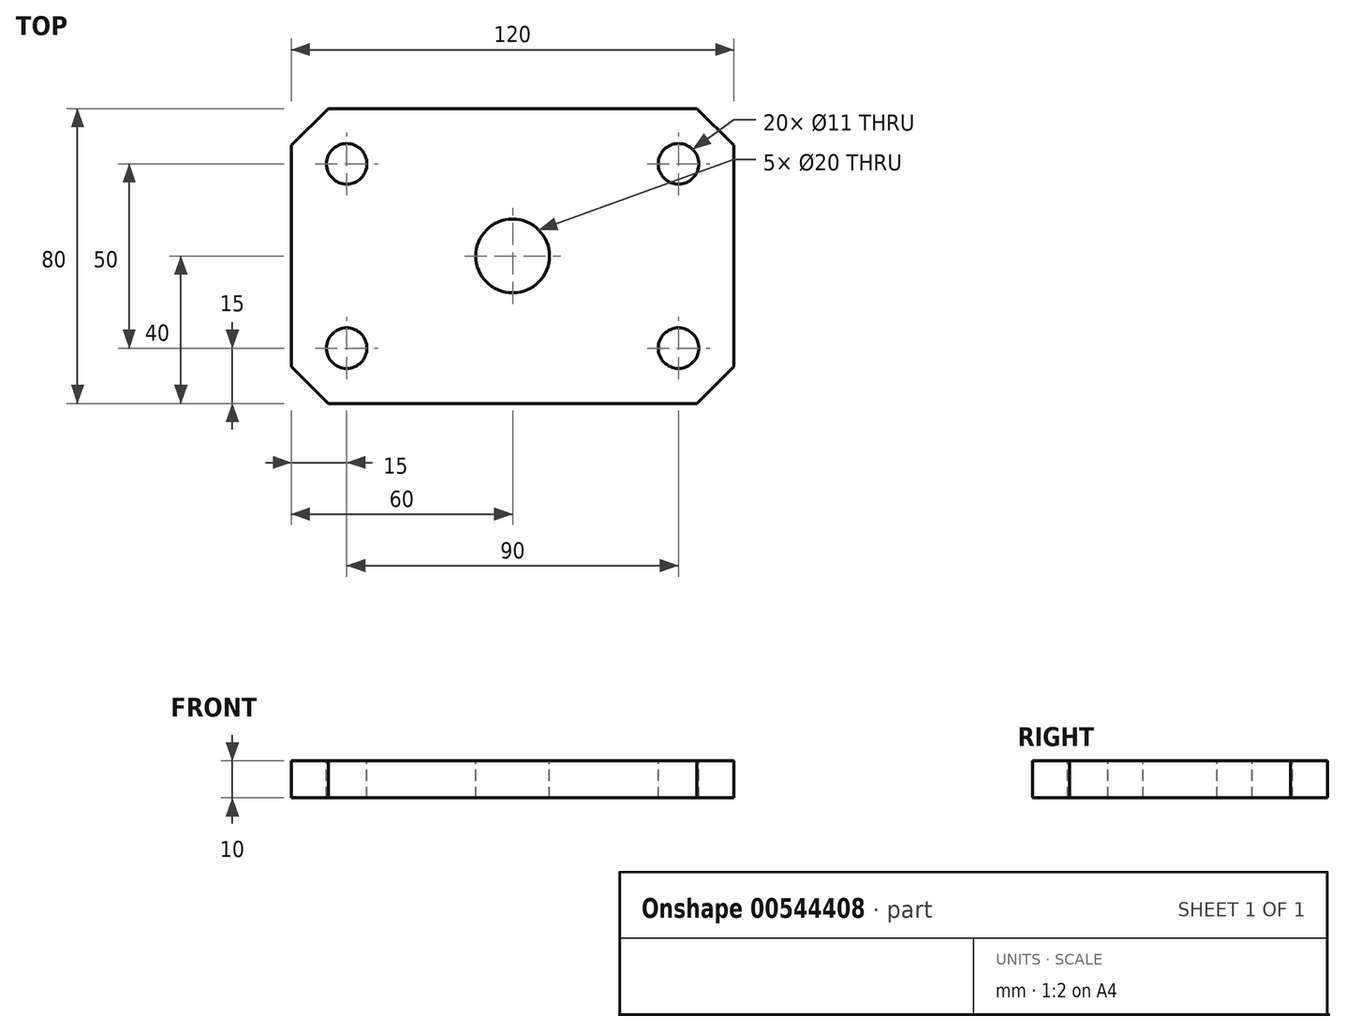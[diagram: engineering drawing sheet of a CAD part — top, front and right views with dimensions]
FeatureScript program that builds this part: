
annotation { "Feature Type Name" : "Feature", "Feature Type Description" : "" }
export const myFeature = defineFeature(function(context is Context, id is Id, definition is map)
    precondition{}
    {
        {
            var Q0;
            Q0=qCreatedBy(makeId("Top.planeOp"),FACE);
            var sketch = newSketch(context, id + "F0", { "sketchPlane" : qUnion([Q0])});
            skLineSegment(sketch, "E0.bottom", {"start": v(-60, 40) * mm, "end": v(60, 40) * mm});
            skLineSegment(sketch, "E0.top", {"start": v(-60, -40) * mm, "end": v(60, -40) * mm});
            skLineSegment(sketch, "E0.left", {"start": v(-60, 40) * mm, "end": v(-60, -40) * mm});
            skLineSegment(sketch, "E0.right", {"start": v(60, 40) * mm, "end": v(60, -40) * mm});
            skPoint(sketch, "E0.middle", {"position": v(0, 0) * mm});
            skSolve(sketch);
        }
        {
            var Q0;
            Q0 = qSketchRegion(id + "F0", true);
            extrude(context, id + "F1", {"entities" : qUnion([Q0]), "endBound" : BoundingType.SYMMETRIC, "depth" : 10 * mm, "offsetDistance" : 25 * mm});
        }
        {
            var Q0;
            Q0=makeQuery(id+"F1.opExtrude","CAP_FACE",FACE,{"disambiguationData":[OSD([sQuery(id+"F0.wireOp",EDGE,"E0.bottom"),sQuery(id+"F0.wireOp",EDGE,"E0.top"),sQuery(id+"F0.wireOp",EDGE,"E0.left"),sQuery(id+"F0.wireOp",EDGE,"E0.right")])],"isStart":false});
            var sketch = newSketch(context, id + "F2", { "sketchPlane" : qUnion([Q0])});
            skLineSegment(sketch, "E1.bottom", {"start": v(-45, 25) * mm, "end": v(45, 25) * mm, "construction": true});
            skLineSegment(sketch, "E1.top", {"start": v(-45, -25) * mm, "end": v(45, -25) * mm, "construction": true});
            skLineSegment(sketch, "E1.left", {"start": v(-45, 25) * mm, "end": v(-45, -25) * mm, "construction": true});
            skLineSegment(sketch, "E1.right", {"start": v(45, 25) * mm, "end": v(45, -25) * mm, "construction": true});
            skPoint(sketch, "E1.middle", {"position": v(0, 0) * mm});
            skSolve(sketch);
        }
        {
            var Q0;
            Q0=sQuery(id+"F2.wireOp",VERTEX,"E1.left.start");
            var Q1;
            Q1=sQuery(id+"F2.wireOp",VERTEX,"E1.right.start");
            var Q2;
            Q2=sQuery(id+"F2.wireOp",VERTEX,"E1.top.end");
            var Q3;
            Q3=sQuery(id+"F2.wireOp",VERTEX,"E1.left.end");
            var Q4;
            Q4=makeQuery(id+"F1.opExtrude","SWEPT_BODY",BODY,{"disambiguationData":[OSD([sQuery(id+"F0.wireOp",EDGE,"E0.bottom"),sQuery(id+"F0.wireOp",EDGE,"E0.top"),sQuery(id+"F0.wireOp",EDGE,"E0.left"),sQuery(id+"F0.wireOp",EDGE,"E0.right")])]});
            hole(context, id + "F3", {"style" : HoleStyle.SIMPLE, "endStyle" : HoleEndStyle.THROUGH, "standardTappedOrClearance" : lookupTablePath({ "standard" : "ISO", "fit" : "Normal", "size" : "M10", "type" : "Clearance" }), "standardBlindInLast" : lookupTablePath({ "fit" : "Standard", "standard" : "ISO", "size" : "M10", "type" : "Clearance" }), "holeDiameter" : 11 * mm, "isTappedThrough" : true, "tappedDepth" : 12 * mm, "tapClearance" : 3, "locations" : qUnion([Q0, Q1, Q2, Q3]), "scope" : qUnion([Q4])});
        }
        {
            var Q0;
            Q0=sQuery(id+"F2.wireOp",VERTEX,"E1.middle");
            var Q1;
            Q1=makeQuery(id+"F1.opExtrude","SWEPT_BODY",BODY,{"disambiguationData":[OSD([sQuery(id+"F0.wireOp",EDGE,"E0.bottom"),sQuery(id+"F0.wireOp",EDGE,"E0.top"),sQuery(id+"F0.wireOp",EDGE,"E0.left"),sQuery(id+"F0.wireOp",EDGE,"E0.right")])]});
            hole(context, id + "F4", {"style" : HoleStyle.SIMPLE, "endStyle" : HoleEndStyle.THROUGH, "standardTappedOrClearance" : lookupTablePath({ "standard" : "ISO", "size" : "20", "type" : "Drilled" }), "standardBlindInLast" : lookupTablePath({ "standard" : "ISO", "size" : "20", "type" : "Drilled" }), "holeDiameter" : 20 * mm, "isTappedThrough" : true, "tappedDepth" : 12 * mm, "tapClearance" : 3, "locations" : qUnion([Q0]), "scope" : qUnion([Q1])});
        }
        {
            var Q0;
            Q0=makeQuery(id+"F1.opExtrude","SWEPT_EDGE",EDGE,{"disambiguationData":[OSD([sQuery(id+"F0.wireOp",EDGE,"E0.top"),sQuery(id+"F0.wireOp",EDGE,"E0.left")])]});
            var Q1;
            Q1=makeQuery(id+"F1.opExtrude","SWEPT_EDGE",EDGE,{"disambiguationData":[OSD([sQuery(id+"F0.wireOp",EDGE,"E0.bottom"),sQuery(id+"F0.wireOp",EDGE,"E0.left")])]});
            var Q2;
            Q2=makeQuery(id+"F1.opExtrude","SWEPT_EDGE",EDGE,{"disambiguationData":[OSD([sQuery(id+"F0.wireOp",EDGE,"E0.top"),sQuery(id+"F0.wireOp",EDGE,"E0.right")])]});
            var Q3;
            Q3=makeQuery(id+"F1.opExtrude","SWEPT_EDGE",EDGE,{"disambiguationData":[OSD([sQuery(id+"F0.wireOp",EDGE,"E0.bottom"),sQuery(id+"F0.wireOp",EDGE,"E0.right")])]});
            chamfer(context, id + "F5", {"entities" : qUnion([Q0, Q1, Q2, Q3]), "width" : 10 * mm, "tangentPropagation" : true});
        }
    });
